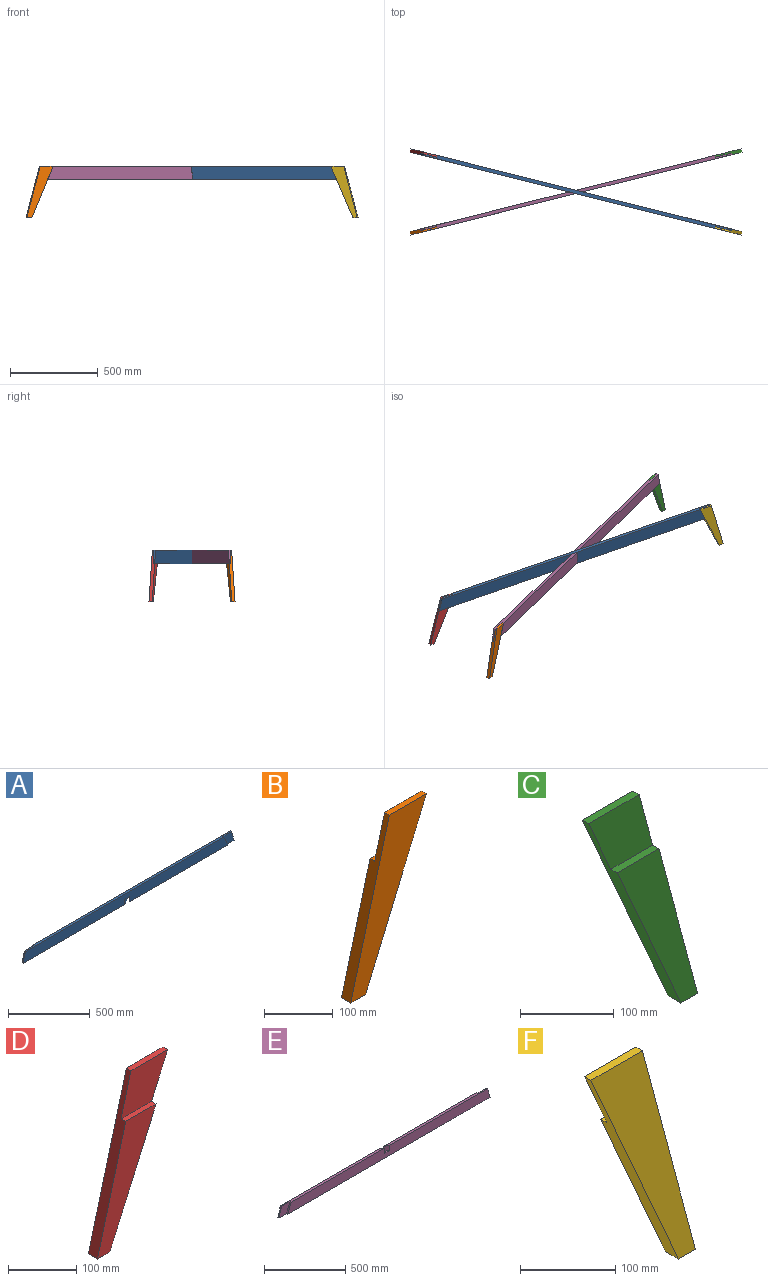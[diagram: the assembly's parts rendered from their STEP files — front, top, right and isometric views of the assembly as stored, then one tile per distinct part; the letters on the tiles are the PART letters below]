
ASSEMBLY  parts=6 mates=4
PART A: 14 faces, bbox 1828.8x19.1x76.2 mm
  f0: plane 912.02x19.05mm, normal (0,0,-1), area 16433.2mm2, adj f1,f3,f4,f7,f8,f11
  f1: plane 1765.75x76.2mm, normal (0,-1,0), area 130950.9mm2, adj f0,f2,f4,f5,f9,f11,f12,f13
  f2: plane 1787.96x19.05mm, normal (0,0,1), area 32609.1mm2, adj f1,f3,f4,f6,f7,f8,f9,f10
  f3: plane 1765.75x76.2mm, normal (0,1,0), area 130950.9mm2, adj f0,f2,f5,f6,f7,f11,f12,f13
  f4: plane 76.2x20.42mm, normal (-0.97,0,0.26), area 751.4mm2, adj f0,f1,f2,f8
  f5: plane 912.02x19.05mm, normal (0,0,-1), area 16433.2mm2, adj f1,f3,f6,f9,f10,f12
  f6: plane 76.2x20.42mm, normal (0.97,0,0.26), area 751.4mm2, adj f2,f3,f5,f10
  f7: plane 76.2x33.57mm, normal (-0.92,0,0.4), area 793.1mm2, adj f0,f2,f3,f8
  f8: plane 96.62x76.2mm, normal (0,1,0), area 5305.5mm2, adj f0,f2,f4,f7
  f9: plane 76.2x33.57mm, normal (0.92,0,0.4), area 793.1mm2, adj f1,f2,f5,f10
  f10: plane 96.62x76.2mm, normal (0,-1,0), area 5305.5mm2, adj f2,f5,f6,f9
  f11: plane 38.1x35.72mm, normal (0.47,-0.88,0), area 1542.3mm2, adj f0,f1,f3,f13
  f12: plane 38.1x35.72mm, normal (-0.47,0.88,0), area 1542.3mm2, adj f1,f3,f5,f13
  f13: plane 76.2x19.05mm, normal (0,0,-1), area 771.2mm2, adj f1,f3,f11,f12
PART B: 8 faces, bbox 155.1x19.1x294.4 mm
  f0: plane 76.2x9.53mm, normal (0,0,1), area 725.8mm2, adj f1,f2,f5,f6
  f1: plane 294.41x78.89mm, normal (-0.97,0,0.26), area 5055mm2, adj f0,f3,f4,f5,f6,f7
  f2: plane 294.41x124.97mm, normal (0.92,0,-0.39), area 5304.5mm2, adj f0,f3,f4,f5,f6,f7
  f3: plane 218.21x122.74mm, normal (0,1,0), area 10298.6mm2, adj f1,f2,f4,f7
  f4: plane 30.12x19.05mm, normal (0,0,-1), area 573.7mm2, adj f1,f2,f3,f5
  f5: plane 294.41x155.09mm, normal (0,-1,0), area 15650.6mm2, adj f0,f1,f2,f4
  f6: plane 96.62x76.2mm, normal (0,1,0), area 5352mm2, adj f0,f1,f2,f7
  f7: plane 64.27x9.53mm, normal (0,0,1), area 612.2mm2, adj f1,f2,f3,f6
PART C: 8 faces, bbox 155.1x19.1x294.4 mm
  f0: plane 76.2x9.53mm, normal (0,0,1), area 725.8mm2, adj f1,f2,f5,f6
  f1: plane 294.41x78.89mm, normal (0.97,0,0.26), area 5055mm2, adj f0,f3,f4,f5,f6,f7
  f2: plane 294.41x129.69mm, normal (-0.92,0,-0.4), area 5335.5mm2, adj f0,f3,f4,f5,f6,f7
  f3: plane 218.21x121.52mm, normal (0,-1,0), area 9650.7mm2, adj f1,f2,f4,f7
  f4: plane 25.4x19.05mm, normal (0,0,-1), area 483.9mm2, adj f1,f2,f3,f5
  f5: plane 294.41x155.09mm, normal (0,1,0), area 14956.2mm2, adj f0,f1,f2,f4
  f6: plane 96.62x76.2mm, normal (0,-1,0), area 5305.5mm2, adj f0,f1,f2,f7
  f7: plane 63.05x9.53mm, normal (0,0,1), area 600.6mm2, adj f1,f2,f3,f6
PART D: 8 faces, bbox 155.1x19.1x294.4 mm
  f0: plane 76.2x9.53mm, normal (0,0,1), area 725.8mm2, adj f1,f2,f5,f6
  f1: plane 294.41x78.89mm, normal (-0.97,0,0.26), area 5055mm2, adj f0,f3,f4,f5,f6,f7
  f2: plane 294.41x129.69mm, normal (0.92,0,-0.4), area 5335.5mm2, adj f0,f3,f4,f5,f6,f7
  f3: plane 218.21x121.52mm, normal (0,-1,0), area 9650.7mm2, adj f1,f2,f4,f7
  f4: plane 25.4x19.05mm, normal (0,0,-1), area 483.9mm2, adj f1,f2,f3,f5
  f5: plane 294.41x155.09mm, normal (0,1,0), area 14956.2mm2, adj f0,f1,f2,f4
  f6: plane 96.62x76.2mm, normal (0,-1,0), area 5305.5mm2, adj f0,f1,f2,f7
  f7: plane 63.05x9.53mm, normal (0,0,1), area 600.6mm2, adj f1,f2,f3,f6
PART E: 14 faces, bbox 1828.8x19.1x76.2 mm
  f0: plane 891.6x19.05mm, normal (0,0,1), area 15919mm2, adj f2,f5,f6,f7,f8,f11
  f1: plane 891.6x19.05mm, normal (0,0,1), area 15919mm2, adj f2,f3,f5,f9,f10,f12
  f2: plane 1765.75x76.2mm, normal (0,-1,0), area 130950.9mm2, adj f0,f1,f3,f4,f7,f11,f12,f13
  f3: plane 76.2x20.42mm, normal (0.97,0,0.26), area 751.4mm2, adj f1,f2,f4,f10
  f4: plane 1828.8x19.05mm, normal (0,0,-1), area 33637.5mm2, adj f2,f3,f5,f6,f7,f8,f9,f10
  f5: plane 1765.75x76.2mm, normal (0,1,0), area 130950.9mm2, adj f0,f1,f4,f6,f9,f11,f12,f13
  f6: plane 76.2x20.42mm, normal (-0.97,0,0.26), area 751.4mm2, adj f0,f4,f5,f8
  f7: plane 76.2x33.57mm, normal (-0.92,0,0.4), area 793.1mm2, adj f0,f2,f4,f8
  f8: plane 96.62x76.2mm, normal (0,-1,0), area 5305.5mm2, adj f0,f4,f6,f7
  f9: plane 76.2x33.57mm, normal (0.92,0,0.4), area 793.1mm2, adj f1,f4,f5,f10
  f10: plane 96.62x76.2mm, normal (0,1,0), area 5305.5mm2, adj f1,f3,f4,f9
  f11: plane 38.1x35.72mm, normal (0.47,0.88,0), area 1542.3mm2, adj f0,f2,f5,f13
  f12: plane 38.1x35.72mm, normal (-0.47,-0.88,0), area 1542.3mm2, adj f1,f2,f5,f13
  f13: plane 76.2x19.05mm, normal (0,0,1), area 771.2mm2, adj f2,f5,f11,f12
PART F: 8 faces, bbox 155.1x19.1x294.4 mm
  f0: plane 76.2x9.53mm, normal (0,0,1), area 725.8mm2, adj f1,f2,f5,f6
  f1: plane 294.41x78.89mm, normal (0.97,0,0.26), area 5055mm2, adj f0,f3,f4,f5,f6,f7
  f2: plane 294.41x129.69mm, normal (-0.92,0,-0.4), area 5335.5mm2, adj f0,f3,f4,f5,f6,f7
  f3: plane 218.21x121.52mm, normal (0,1,0), area 9650.7mm2, adj f1,f2,f4,f7
  f4: plane 25.4x19.05mm, normal (0,0,-1), area 483.9mm2, adj f1,f2,f3,f5
  f5: plane 294.41x155.09mm, normal (0,-1,0), area 14956.2mm2, adj f0,f1,f2,f4
  f6: plane 96.62x76.2mm, normal (0,1,0), area 5305.5mm2, adj f0,f1,f2,f7
  f7: plane 63.05x9.53mm, normal (0,0,1), area 600.6mm2, adj f1,f2,f3,f6
PLACE A rot(axis=(0,0,-1),14deg) t=(-138.72,54.01,38.1)mm
PLACE B rot(axis=(0,0,1),14deg) t=(-795.74,-179.57,38.1)mm
PLACE C rot(axis=(0,0,1),14deg) t=(795.61,198.62,38.1)mm
PLACE D rot(axis=(0,0,-1),14deg) t=(-795.74,198.63,38.1)mm
PLACE E rot(axis=(0,0,1),14deg) t=(-141.03,-25.71,38.1)mm
PLACE F rot(axis=(0,0,-1),14deg) t=(795.61,-179.57,38.1)mm
MATE fastened C.f6 <-> E.f10  axis (0.24,-0.97,0) through (867.23,226.35,38.1)mm
MATE fastened D.f6 <-> A.f8  axis (-0.24,-0.97,0) through (-867.35,226.35,38.1)mm
MATE fastened A.f10 <-> F.f6  axis (-0.24,-0.97,0) through (867.23,-207.29,38.1)mm
MATE fastened E.f8 <-> B.f6  axis (0.24,-0.97,0) through (-867.36,-207.29,38.1)mm
